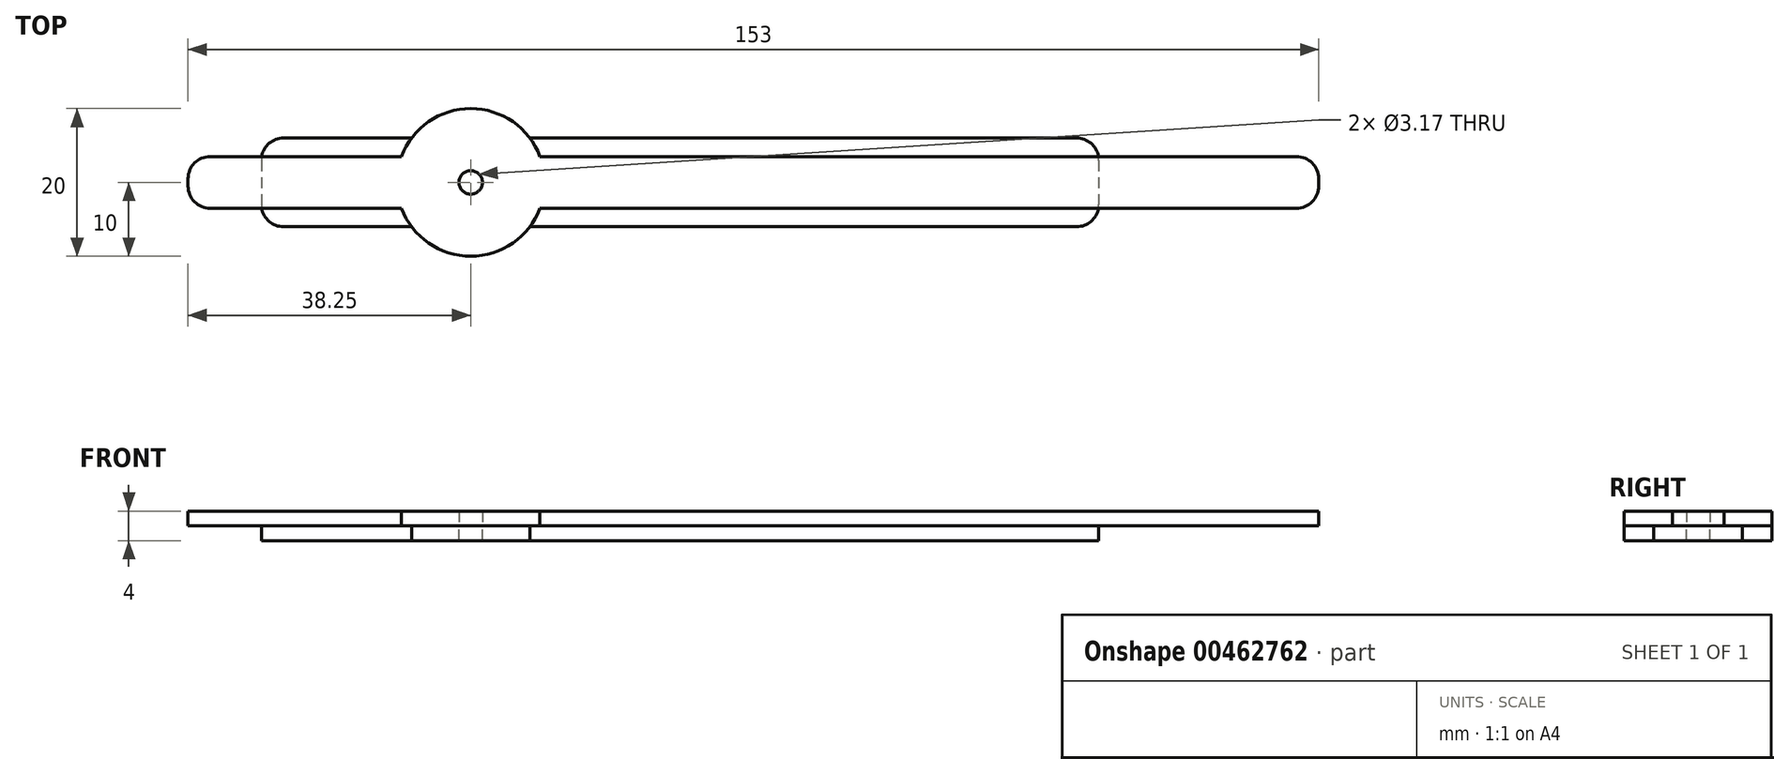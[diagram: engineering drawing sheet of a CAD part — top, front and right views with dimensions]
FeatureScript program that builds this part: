
annotation { "Feature Type Name" : "Feature", "Feature Type Description" : "" }
export const myFeature = defineFeature(function(context is Context, id is Id, definition is map)
    precondition{}
    {
        {
            var Q0;
            Q0=qCreatedBy(makeId("Top.planeOp"),FACE);
            var sketch = newSketch(context, id + "F0", { "sketchPlane" : qUnion([Q0])});
            skCircle(sketch, "E0", {"center": v(0, 0) * mm, "radius": 1.59 * mm});
            skLineSegment(sketch, "E1.bottom", {"start": v(-38.25, 3.5) * mm, "end": v(114.75, 3.5) * mm});
            skLineSegment(sketch, "E1.top", {"start": v(-38.25, -3.5) * mm, "end": v(114.75, -3.5) * mm});
            skLineSegment(sketch, "E1.left", {"start": v(-38.25, 3.5) * mm, "end": v(-38.25, -3.5) * mm});
            skLineSegment(sketch, "E1.right", {"start": v(114.75, 3.5) * mm, "end": v(114.75, -3.5) * mm});
            skCircle(sketch, "E2", {"center": v(0, 0) * mm, "radius": 10 * mm});
            skSolve(sketch);
        }
        {
            var Q0;
            Q0=qSketchRegion(id+"F0",true);
            extrude(context, id + "F1", {"entities" : qUnion([Q0]), "depth" : 2 * mm});
        }
        {
            var Q0;
            Q0=qCreatedBy(makeId("Top.planeOp"),FACE);
            var sketch = newSketch(context, id + "F2", { "sketchPlane" : qUnion([Q0])});
            skCircle(sketch, "E3", {"center": v(0, 0) * mm, "radius": 1.59 * mm});
            skLineSegment(sketch, "E4.bottom", {"start": v(-28.33, 6) * mm, "end": v(85, 6) * mm});
            skLineSegment(sketch, "E4.top", {"start": v(-28.33, -6) * mm, "end": v(85, -6) * mm});
            skLineSegment(sketch, "E4.left", {"start": v(-28.33, 6) * mm, "end": v(-28.33, -6) * mm});
            skLineSegment(sketch, "E4.right", {"start": v(85, 6) * mm, "end": v(85, -6) * mm});
            skCircle(sketch, "E5", {"center": v(0, 0) * mm, "radius": 10 * mm});
            skSolve(sketch);
        }
        {
            var Q0;
            Q0=qSketchRegion(id+"F2",true);
            extrude(context, id + "F3", {"entities" : qUnion([Q0]), "oppositeDirection" : true, "depth" : 2 * mm});
        }
        {
            var Q0;
            Q0=makeQuery(id+"F1.opExtrude","SWEPT_EDGE",EDGE,{"disambiguationData":[OSD([sQuery(id+"F0.wireOp",EDGE,"E1.bottom"),sQuery(id+"F0.wireOp",EDGE,"E1.left")])]});
            var Q1;
            Q1=makeQuery(id+"F3.opExtrude","SWEPT_EDGE",EDGE,{"disambiguationData":[OSD([sQuery(id+"F2.wireOp",EDGE,"E4.bottom"),sQuery(id+"F2.wireOp",EDGE,"E4.left")])]});
            var Q2;
            Q2=makeQuery(id+"F3.opExtrude","SWEPT_EDGE",EDGE,{"disambiguationData":[OSD([sQuery(id+"F2.wireOp",EDGE,"E4.top"),sQuery(id+"F2.wireOp",EDGE,"E4.left")])]});
            var Q3;
            Q3=makeQuery(id+"F1.opExtrude","SWEPT_EDGE",EDGE,{"disambiguationData":[OSD([sQuery(id+"F0.wireOp",EDGE,"E1.top"),sQuery(id+"F0.wireOp",EDGE,"E1.left")])]});
            var Q4;
            Q4=makeQuery(id+"F1.opExtrude","SWEPT_EDGE",EDGE,{"disambiguationData":[OSD([sQuery(id+"F0.wireOp",EDGE,"E1.top"),sQuery(id+"F0.wireOp",EDGE,"E1.right")])]});
            var Q5;
            Q5=makeQuery(id+"F3.opExtrude","SWEPT_EDGE",EDGE,{"disambiguationData":[OSD([sQuery(id+"F2.wireOp",EDGE,"E4.top"),sQuery(id+"F2.wireOp",EDGE,"E4.right")])]});
            var Q6;
            Q6=makeQuery(id+"F1.opExtrude","SWEPT_EDGE",EDGE,{"disambiguationData":[OSD([sQuery(id+"F0.wireOp",EDGE,"E1.bottom"),sQuery(id+"F0.wireOp",EDGE,"E1.right")])]});
            var Q7;
            Q7=makeQuery(id+"F3.opExtrude","SWEPT_EDGE",EDGE,{"disambiguationData":[OSD([sQuery(id+"F2.wireOp",EDGE,"E4.bottom"),sQuery(id+"F2.wireOp",EDGE,"E4.right")])]});
            fillet(context, id + "F4", {"entities" : qUnion([Q0, Q1, Q2, Q3, Q4, Q5, Q6, Q7]), "radius" : 3 * mm, "tangentPropagation" : true, "allowEdgeOverflow" : false});
        }
    });
